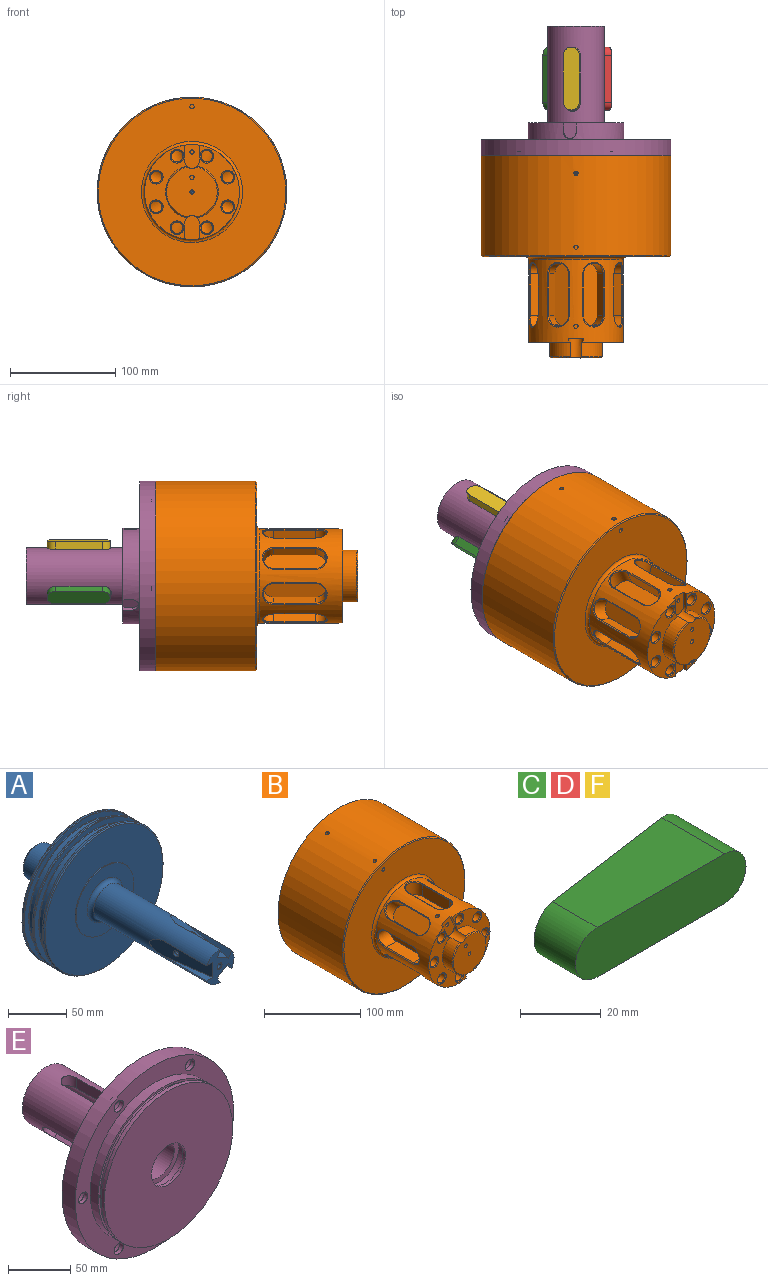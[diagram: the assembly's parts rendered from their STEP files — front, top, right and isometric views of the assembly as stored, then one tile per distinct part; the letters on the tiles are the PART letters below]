
ASSEMBLY  parts=6 mates=5
PART A: 68 faces, bbox 145x224.3x145 mm
  f0: cylinder r=1.5mm len=26.28mm, axis (0,-1,0), area 245.5mm2, adj f1,f2,f3,f4,f5,f6,f65
  f1: cylinder r=1.5mm len=11.87mm, axis (-0.99,-0.14,0), area 97.1mm2, adj f0,f4,f6,f51
  f2: cylinder r=1.5mm len=11.46mm, axis (0.5,-0.14,0.86), area 97.1mm2, adj f0,f3,f6,f55
  f3: cylinder r=1.5mm len=6.5mm, axis (-0.99,-0.14,0), area 44.4mm2, adj f0,f2,f4,f5,f6,f56
  f4: cylinder r=1.5mm len=6.81mm, axis (0.5,-0.14,0.86), area 44.4mm2, adj f0,f1,f3,f5,f6,f57
  f5: cylinder r=1.5mm len=11.46mm, axis (0.5,-0.14,-0.86), area 97.1mm2, adj f0,f3,f4,f61
  f6: cylinder r=1.5mm len=6.81mm, axis (0.5,-0.14,-0.86), area 44.4mm2, adj f0,f1,f2,f3,f4,f62
  f7: cylinder r=17.48mm len=135mm, axis (0,1,0), area 11728.8mm2, adj f8,f48,f49,f50,f52,f53,f54,f58
  f8: plane 34.95x33.06mm, normal (0,-1,0), area 511.1mm2, adj f7,f48,f49,f50,f52,f53,f54,f58
  f9: cylinder r=1.5mm len=17.25mm, axis (0,0,-1), area 153.3mm2, adj f10,f32,f36
  f10: cylinder r=17.25mm len=34.5mm, axis (0,-1,0), area 2594.2mm2, adj f9,f29,f64
  f11: cylinder r=72.5mm len=145mm, axis (0,1,0), area 774.4mm2, adj f39,f40
  f12: plane 143x143mm, normal (0,-1,0), area 12212.2mm2, adj f26,f39
  f13: plane 144x144mm, normal (0,-1,0), area 2393.1mm2, adj f42,f43
  f14: plane 144x144mm, normal (0,1,0), area 2393.1mm2, adj f40,f41
  f15: cylinder r=66mm len=132mm, axis (0,-1,0), area 3524.9mm2, adj f41,f42
  f16: cylinder r=72.5mm len=145mm, axis (0,1,0), area 728.8mm2, adj f43,f44
  f17: plane 144x144mm, normal (0,-1,0), area 2393.1mm2, adj f46,f47
  f18: plane 144x144mm, normal (0,1,0), area 2393.1mm2, adj f44,f45
  f19: cylinder r=66mm len=132mm, axis (0,-1,0), area 3524.9mm2, adj f45,f46
  f20: cylinder r=72.5mm len=145mm, axis (0,1,0), area 774.4mm2, adj f38,f47
  f21: plane 143x143mm, normal (0,1,0), area 2582.4mm2, adj f22,f38
  f22: cylinder r=65.5mm len=131mm, axis (0,-1,0), area 535mm2, adj f21,f23
  f23: plane 131x131mm, normal (0,1,0), area 3091.3mm2, adj f22,f24
  f24: cylinder r=57.5mm len=115mm, axis (0,1,0), area 2529mm2, adj f23,f25
  f25: plane 115x115mm, normal (0,1,0), area 9098.6mm2, adj f24,f64
  f26: cylinder r=35mm len=70mm, axis (0,1,0), area 219.9mm2, adj f12,f27
  f27: plane 70x70mm, normal (0,-1,0), area 2399.6mm2, adj f26,f63
  f28: cylinder r=17.48mm len=34.95mm, axis (0,1,0), area 3403.8mm2, adj f29,f31
  f29: plane 34.95x34.95mm, normal (0,-1,0), area 24.5mm2, adj f10,f28
  f30: plane 26.95x26.95mm, normal (0,1,0), area 550.8mm2, adj f31,f33
  f31: cone r=13.48mm half-angle=45deg, axis (0,-1,0), area 550mm2, adj f28,f30
  f32: cylinder r=1.5mm len=56mm, axis (0,1,0), area 518.8mm2, adj f9,f33,f35
  f33: cone r=1.5mm half-angle=45deg, axis (0,1,0), area 17.8mm2, adj f30,f32
  f34: cone r=0mm half-angle=59deg, axis (0,0,-1), area 8.2mm2, adj f35
  f35: cylinder r=1.5mm len=3mm, axis (0,0,-1), area 17.5mm2, adj f32,f34,f36
  f36: cylinder r=1.5mm len=13mm, axis (0,1,0), area 113.5mm2, adj f9,f35,f37
  f37: cone r=0mm half-angle=59deg, axis (0,1,0), area 8.2mm2, adj f36
  f38: cone r=72.5mm half-angle=45deg, axis (0,-1,0), area 639.8mm2, adj f20,f21
  f39: cone r=71.5mm half-angle=45deg, axis (0,1,0), area 639.8mm2, adj f11,f12
  f40: cone r=72.5mm half-angle=45deg, axis (0,-1,0), area 321mm2, adj f11,f14
  f41: cone r=66.5mm half-angle=45deg, axis (0,-1,0), area 294.3mm2, adj f14,f15
  f42: cone r=66mm half-angle=45deg, axis (0,1,0), area 294.3mm2, adj f13,f15
  f43: cone r=72mm half-angle=45deg, axis (0,1,0), area 321mm2, adj f13,f16
  f44: cone r=72.5mm half-angle=45deg, axis (0,-1,0), area 321mm2, adj f16,f18
  f45: cone r=66.5mm half-angle=45deg, axis (0,-1,0), area 294.3mm2, adj f18,f19
  f46: cone r=66mm half-angle=45deg, axis (0,1,0), area 294.3mm2, adj f17,f19
  f47: cone r=72mm half-angle=45deg, axis (0,1,0), area 321mm2, adj f17,f20
  f48: plane 53.99x7.59mm, normal (0,0,1), area 204.8mm2, adj f7,f8,f50
  f49: plane 53.99x7.59mm, normal (0,0,-1), area 204.8mm2, adj f7,f8,f50
  f50: plane 67.42x15.8mm, normal (-0.99,-0.14,0), area 977.6mm2, adj f7,f8,f48,f49,f51
  f51: cone r=1.5mm half-angle=45deg, axis (-0.99,-0.14,0), area 30mm2, adj f1,f50
  f52: plane 53.99x6.57mm, normal (0.87,0,-0.5), area 204.8mm2, adj f7,f8,f54
  f53: plane 53.99x6.57mm, normal (-0.87,0,0.5), area 204.8mm2, adj f7,f8,f54
  f54: plane 67.42x17.48mm, normal (0.5,-0.14,0.86), area 977.6mm2, adj f7,f8,f52,f53,f55
  f55: cone r=1.5mm half-angle=45deg, axis (0.5,-0.14,0.86), area 30mm2, adj f2,f54
  f56: cone r=0mm half-angle=59deg, axis (-0.99,-0.14,0), area 8.2mm2, adj f3
  f57: cone r=0mm half-angle=59deg, axis (0.5,-0.14,0.86), area 8.2mm2, adj f4
  f58: plane 53.99x6.57mm, normal (-0.87,0,-0.5), area 204.8mm2, adj f7,f8,f60
  f59: plane 53.99x6.57mm, normal (0.87,0,0.5), area 204.8mm2, adj f7,f8,f60
  f60: plane 67.42x17.48mm, normal (0.5,-0.14,-0.86), area 977.6mm2, adj f7,f8,f58,f59,f61
  f61: cone r=1.5mm half-angle=45deg, axis (0.5,-0.14,-0.86), area 30mm2, adj f5,f60
  f62: cone r=0mm half-angle=59deg, axis (0.5,-0.14,-0.86), area 8.2mm2, adj f6
  f63: torus R=21.48mm, axis (0,-1,0), area 747.3mm2, adj f7,f27
  f64: torus R=20.25mm, axis (0,1,0), area 543mm2, adj f10,f25
  f65: cone r=0mm half-angle=59deg, axis (0,-1,0), area 14.7mm2, adj f0,f66
  f66: cylinder r=2.5mm len=12.5mm, axis (0,-1,0), area 196.3mm2, adj f65,f67
  f67: cone r=2.5mm half-angle=45deg, axis (0,-1,0), area 12.2mm2, adj f8,f66
PART B: 156 faces, bbox 180x192x180 mm
  f0: cylinder r=2mm len=7.96mm, axis (-0.38,0,0.92), area 87.4mm2, adj f11,f123,f128
  f1: cylinder r=2mm len=41.26mm, axis (-0.38,0,0.92), area 510.5mm2, adj f2,f122,f123,f127
  f2: cylinder r=2mm len=9mm, axis (0,-1,0), area 99.3mm2, adj f1,f7,f121
  f3: cylinder r=2mm len=30mm, axis (0,-1,0), area 377mm2, adj f14,f112,f115
  f4: plane 83.39x55.54mm, normal (0,-1,0), area 1392.8mm2, adj f5,f11,f69,f80,f91,f102,f105,f106
  f5: cylinder r=25mm len=45.67mm, axis (0,1,0), area 956.4mm2, adj f4,f106,f110,f135
  f6: cylinder r=90mm len=180mm, axis (0,1,0), area 53695.6mm2, adj f9,f117,f121,f155
  f7: plane 178x178mm, normal (0,-1,0), area 17633.8mm2, adj f2,f134,f155
  f8: cylinder r=73mm len=146mm, axis (0,-1,0), area 30260.1mm2, adj f120,f132,f133
  f9: plane 180x180mm, normal (0,1,0), area 7304.2mm2, adj f6,f132,f138,f141,f144,f147,f150,f153
  f10: plane 140x140mm, normal (0,1,0), area 14318.6mm2, adj f131,f133
  f11: cylinder r=45mm len=90mm, axis (0,1,0), area 11744.7mm2, adj f0,f4,f12,f20,f21,f22,f23,f31
  f12: plane 83.39x55.54mm, normal (0,-1,0), area 1392.8mm2, adj f11,f13,f25,f36,f47,f58,f104,f106
  f13: cylinder r=25mm len=45.67mm, axis (0,1,0), area 956.4mm2, adj f12,f106,f110,f136
  f14: plane 48x48mm, normal (0,-1,0), area 1765.4mm2, adj f3,f106,f110,f111,f135,f136
  f15: cylinder r=10.1mm len=20.2mm, axis (0,0,1), area 470.9mm2, adj f16,f18,f19,f20
  f16: plane 39.8x14.84mm, normal (1,0,0), area 590.6mm2, adj f15,f17,f19,f22
  f17: cylinder r=10.1mm len=20.2mm, axis (0,0,1), area 371.8mm2, adj f16,f18,f19,f23,f24
  f18: plane 39.8x14.84mm, normal (-1,0,0), area 590.6mm2, adj f15,f17,f19,f21
  f19: plane 60x20.2mm, normal (0,0,1), area 1124.4mm2, adj f15,f16,f17,f18
  f20: bspline ~22.19x10.89mm, area 39.7mm2, adj f11,f15,f21,f22
  f21: plane 39.8x0.99mm, normal (-0.61,0,0.79), area 50mm2, adj f11,f18,f20,f23
  f22: plane 39.8x0.99mm, normal (0.61,0,0.79), area 50mm2, adj f11,f16,f20,f23
  f23: bspline ~22.18x10.89mm, area 39.7mm2, adj f11,f17,f21,f22
  f24: cylinder r=5.5mm len=14mm, axis (0,-1,0), area 483.8mm2, adj f17,f25
  f25: cone r=5.5mm half-angle=45deg, axis (0,-1,0), area 53.3mm2, adj f12,f24
  f26: cylinder r=10.1mm len=24.78mm, axis (0.71,0,0.71), area 470.9mm2, adj f27,f29,f30,f31
  f27: plane 39.8x10.49mm, normal (0.71,0,-0.71), area 590.6mm2, adj f26,f28,f30,f33
  f28: cylinder r=10.1mm len=24.78mm, axis (0.71,0,0.71), area 371.8mm2, adj f27,f29,f30,f34,f35
  f29: plane 39.8x10.49mm, normal (-0.71,0,0.71), area 590.6mm2, adj f26,f28,f30,f32
  f30: plane 60x14.28mm, normal (0.71,0,0.71), area 1124.4mm2, adj f26,f27,f28,f29
  f31: bspline ~15.69x15.69mm, area 39.7mm2, adj f11,f26,f32,f33
  f32: plane 39.8x1.25mm, normal (0.12,0,0.99), area 50mm2, adj f11,f29,f31,f34
  f33: plane 39.8x1.25mm, normal (0.99,0,0.12), area 50mm2, adj f11,f27,f31,f34
  f34: bspline ~15.69x15.69mm, area 39.7mm2, adj f11,f28,f32,f33
  f35: cylinder r=5.5mm len=14.78mm, axis (0,-1,0), area 510.7mm2, adj f28,f36
  f36: cone r=5.5mm half-angle=45deg, axis (0,-1,0), area 53.3mm2, adj f12,f35
  f37: cylinder r=10.1mm len=20.2mm, axis (1,0,0), area 470.9mm2, adj f38,f40,f41,f42
  f38: plane 39.8x14.84mm, normal (0,0,-1), area 590.6mm2, adj f37,f39,f41,f44
  f39: cylinder r=10.1mm len=20.2mm, axis (1,0,0), area 371.8mm2, adj f38,f40,f41,f45,f46
  f40: plane 39.8x14.84mm, normal (0,0,1), area 590.6mm2, adj f37,f39,f41,f43
  f41: plane 60x20.2mm, normal (1,0,0), area 1124.4mm2, adj f37,f38,f39,f40
  f42: bspline ~22.18x10.9mm, area 39.7mm2, adj f11,f37,f43,f44
  f43: plane 39.8x0.99mm, normal (0.79,0,0.61), area 50mm2, adj f11,f40,f42,f45
  f44: plane 39.8x0.99mm, normal (0.79,0,-0.61), area 50mm2, adj f11,f38,f42,f45
  f45: bspline ~22.18x10.9mm, area 39.7mm2, adj f11,f39,f43,f44
  f46: cylinder r=5.5mm len=15.63mm, axis (0,-1,0), area 540.1mm2, adj f39,f47
  f47: cone r=5.5mm half-angle=45deg, axis (0,-1,0), area 53.3mm2, adj f12,f46
  f48: cylinder r=10.1mm len=24.78mm, axis (0.71,0,-0.71), area 470.9mm2, adj f49,f51,f52,f53
  f49: plane 39.8x10.49mm, normal (-0.71,0,-0.71), area 590.6mm2, adj f48,f50,f52,f55
  f50: cylinder r=10.1mm len=24.78mm, axis (0.71,0,-0.71), area 371.9mm2, adj f49,f51,f52,f56,f57
  f51: plane 39.8x10.49mm, normal (0.71,0,0.71), area 590.6mm2, adj f48,f50,f52,f54
  f52: plane 60x14.28mm, normal (0.71,0,-0.71), area 1124.4mm2, adj f48,f49,f50,f51
  f53: bspline ~15.69x15.69mm, area 39.7mm2, adj f11,f48,f54,f55
  f54: plane 39.8x1.25mm, normal (0.99,0,-0.12), area 50mm2, adj f11,f51,f53,f56
  f55: plane 39.8x1.25mm, normal (0.12,0,-0.99), area 50mm2, adj f11,f49,f53,f56
  f56: bspline ~15.69x15.69mm, area 39.7mm2, adj f11,f50,f54,f55
  f57: cylinder r=5.5mm len=14.78mm, axis (0,-1,0), area 510.7mm2, adj f50,f58
  f58: cone r=5.5mm half-angle=45deg, axis (0,-1,0), area 53.3mm2, adj f12,f57
  f59: cylinder r=10.1mm len=20.2mm, axis (0,0,-1), area 470.9mm2, adj f60,f62,f63,f64
  f60: plane 39.8x14.84mm, normal (-1,0,0), area 590.6mm2, adj f59,f61,f63,f66
  f61: cylinder r=10.1mm len=20.2mm, axis (0,0,-1), area 371.9mm2, adj f60,f62,f63,f67,f68
  f62: plane 39.8x14.84mm, normal (1,0,0), area 590.6mm2, adj f59,f61,f63,f65
  f63: plane 60x20.2mm, normal (0,0,-1), area 1124.4mm2, adj f59,f60,f61,f62
  f64: bspline ~22.18x10.9mm, area 39.7mm2, adj f11,f59,f65,f66
  f65: plane 39.8x0.99mm, normal (0.61,0,-0.79), area 50mm2, adj f11,f62,f64,f67
  f66: plane 39.8x0.99mm, normal (-0.61,0,-0.79), area 50mm2, adj f11,f60,f64,f67
  f67: bspline ~22.18x10.9mm, area 39.7mm2, adj f11,f61,f65,f66
  f68: cylinder r=5.5mm len=14mm, axis (0,-1,0), area 483.8mm2, adj f61,f69
  f69: cone r=5.5mm half-angle=45deg, axis (0,-1,0), area 53.3mm2, adj f4,f68
  f70: cylinder r=10.1mm len=24.78mm, axis (-0.71,0,-0.71), area 470.9mm2, adj f71,f73,f74,f75
  f71: plane 39.8x10.49mm, normal (-0.71,0,0.71), area 590.6mm2, adj f70,f72,f74,f77
  f72: cylinder r=10.1mm len=24.78mm, axis (-0.71,0,-0.71), area 372mm2, adj f71,f73,f74,f78,f79
  f73: plane 39.8x10.49mm, normal (0.71,0,-0.71), area 590.6mm2, adj f70,f72,f74,f76
  f74: plane 60x14.28mm, normal (-0.71,0,-0.71), area 1124.4mm2, adj f70,f71,f72,f73
  f75: bspline ~15.69x15.69mm, area 39.7mm2, adj f11,f70,f76,f77
  f76: plane 39.8x1.25mm, normal (-0.12,0,-0.99), area 50mm2, adj f11,f73,f75,f78
  f77: plane 39.8x1.25mm, normal (-0.99,0,-0.12), area 50mm2, adj f11,f71,f75,f78
  f78: bspline ~15.69x15.69mm, area 39.7mm2, adj f11,f72,f76,f77
  f79: cylinder r=5.5mm len=14.78mm, axis (0,-1,0), area 510.7mm2, adj f72,f80
  f80: cone r=5.5mm half-angle=45deg, axis (0,-1,0), area 53.3mm2, adj f4,f79
  f81: cylinder r=10.1mm len=20.2mm, axis (-1,0,0), area 470.9mm2, adj f82,f84,f85,f86
  f82: plane 39.8x14.84mm, normal (0,0,1), area 590.6mm2, adj f81,f83,f85,f88
  f83: cylinder r=10.1mm len=20.2mm, axis (-1,0,0), area 372mm2, adj f82,f84,f85,f89,f90
  f84: plane 39.8x14.84mm, normal (0,0,-1), area 590.6mm2, adj f81,f83,f85,f87
  f85: plane 60x20.2mm, normal (-1,0,0), area 1124.4mm2, adj f81,f82,f83,f84
  f86: bspline ~22.18x10.9mm, area 39.7mm2, adj f11,f81,f87,f88
  f87: plane 39.8x0.99mm, normal (-0.79,0,-0.61), area 50mm2, adj f11,f84,f86,f89
  f88: plane 39.8x0.99mm, normal (-0.79,0,0.61), area 50mm2, adj f11,f82,f86,f89
  f89: bspline ~22.18x10.9mm, area 39.7mm2, adj f11,f83,f87,f88
  f90: cylinder r=5.5mm len=15.63mm, axis (0,-1,0), area 540.1mm2, adj f83,f91
  f91: cone r=5.5mm half-angle=45deg, axis (0,-1,0), area 53.3mm2, adj f4,f90
  f92: cylinder r=10.1mm len=24.78mm, axis (-0.71,0,0.71), area 470.9mm2, adj f93,f95,f96,f97
  f93: plane 39.8x10.49mm, normal (0.71,0,0.71), area 590.6mm2, adj f92,f94,f96,f99
  f94: cylinder r=10.1mm len=24.78mm, axis (-0.71,0,0.71), area 371.9mm2, adj f93,f95,f96,f100,f101
  f95: plane 39.8x10.49mm, normal (-0.71,0,-0.71), area 590.6mm2, adj f92,f94,f96,f98
  f96: plane 60x14.28mm, normal (-0.71,0,0.71), area 1124.4mm2, adj f92,f93,f94,f95
  f97: bspline ~15.69x15.69mm, area 39.7mm2, adj f11,f92,f98,f99
  f98: plane 39.8x1.25mm, normal (-0.99,0,0.12), area 50mm2, adj f11,f95,f97,f100
  f99: plane 39.8x1.25mm, normal (-0.12,0,0.99), area 50mm2, adj f11,f93,f97,f100
  f100: bspline ~15.69x15.69mm, area 39.7mm2, adj f11,f94,f98,f99
  f101: cylinder r=5.5mm len=14.78mm, axis (0,-1,0), area 510.7mm2, adj f94,f102
  f102: cone r=5.5mm half-angle=45deg, axis (0,-1,0), area 53.3mm2, adj f4,f101
  f103: plane 23.68x19.27mm, normal (0,-1,0), area 281.7mm2, adj f11,f104,f105,f106,f128
  f104: plane 14x5.8mm, normal (-0.92,0,-0.38), area 53mm2, adj f11,f12,f103,f106
  f105: plane 14x5.8mm, normal (0.92,0,0.38), area 53mm2, adj f4,f11,f103,f106
  f106: cylinder r=7mm len=18.5mm, axis (0,-1,0), area 246mm2, adj f4,f5,f12,f13,f14,f103,f104,f105
  f107: plane 23.68x19.27mm, normal (0,-1,0), area 294.2mm2, adj f11,f108,f109,f110
  f108: plane 14x5.8mm, normal (0.92,0,0.38), area 53mm2, adj f4,f11,f107,f110
  f109: plane 14x5.8mm, normal (-0.92,0,-0.38), area 53mm2, adj f11,f12,f107,f110
  f110: cylinder r=7mm len=18.5mm, axis (0,-1,0), area 246mm2, adj f4,f5,f12,f13,f14,f107,f108,f109
  f111: cylinder r=2mm len=56mm, axis (0,-1,0), area 703.7mm2, adj f14,f129
  f112: cylinder r=2mm len=23.7mm, axis (-0.38,0,0.92), area 271.8mm2, adj f3,f114,f123,f128
  f113: plane 4x4mm, normal (0,-1,0), area 12.6mm2, adj f114
  f114: cylinder r=2mm len=5mm, axis (0,-1,0), area 62.8mm2, adj f112,f113,f115
  f115: cylinder r=2mm len=4.77mm, axis (-0.38,0,0.92), area 19.2mm2, adj f3,f114,f116
  f116: plane 4x3.7mm, normal (-0.38,0,0.92), area 12.6mm2, adj f115
  f117: cylinder r=2mm len=9.83mm, axis (-0.38,0,0.92), area 112.8mm2, adj f6,f119,f122
  f118: plane 4x4mm, normal (0,-1,0), area 12.6mm2, adj f119
  f119: cylinder r=2mm len=5mm, axis (0,-1,0), area 62.8mm2, adj f117,f118,f120
  f120: cylinder r=2mm len=8.95mm, axis (-0.38,0,0.92), area 100.9mm2, adj f8,f119,f122
  f121: cylinder r=2mm len=9.83mm, axis (-0.38,0,0.92), area 112.8mm2, adj f2,f6,f122
  f122: cylinder r=2mm len=70mm, axis (0,-1,0), area 879.6mm2, adj f1,f117,f120,f121
  f123: cylinder r=2mm len=75mm, axis (0,-1,0), area 942.5mm2, adj f0,f1,f112,f125
  f124: plane 4x3.7mm, normal (-0.38,0,0.92), area 12.6mm2, adj f125
  f125: cylinder r=2mm len=5.15mm, axis (-0.38,0,0.92), area 31.8mm2, adj f123,f124,f127
  f126: plane 4x4mm, normal (0,-1,0), area 12.6mm2, adj f127
  f127: cylinder r=2mm len=5mm, axis (0,-1,0), area 62.8mm2, adj f1,f125,f126
  f128: cylinder r=2mm len=11.5mm, axis (0,-1,0), area 130.7mm2, adj f0,f103,f112
  f129: plane 35x35mm, normal (0,1,0), area 949.5mm2, adj f111,f130
  f130: cylinder r=17.5mm len=56mm, axis (0,1,0), area 6157.5mm2, adj f129,f131
  f131: cone r=18.5mm half-angle=14deg, axis (0,1,0), area 466.3mm2, adj f10,f130
  f132: cone r=75mm half-angle=15.9deg, axis (0,1,0), area 3384.9mm2, adj f8,f9
  f133: torus R=70mm, axis (0,-1,0), area 2129.2mm2, adj f8,f10
  f134: torus R=48mm, axis (0,-1,0), area 1364.7mm2, adj f7,f11
  f135: cone r=24mm half-angle=45deg, axis (0,1,0), area 95.8mm2, adj f5,f14,f106,f110
  f136: cone r=24mm half-angle=45deg, axis (0,1,0), area 95.8mm2, adj f13,f14,f106,f110
  f137: cylinder r=4.3mm len=36.3mm, axis (0,1,0), area 980.7mm2, adj f138,f139
  f138: cone r=4.3mm half-angle=45deg, axis (0,1,0), area 28.9mm2, adj f9,f137
  f139: cone r=0mm half-angle=59deg, axis (0,1,0), area 67.8mm2, adj f137
  f140: cylinder r=4.3mm len=36.3mm, axis (0,1,0), area 980.7mm2, adj f141,f142
  f141: cone r=4.3mm half-angle=45deg, axis (0,1,0), area 28.9mm2, adj f9,f140
  f142: cone r=0mm half-angle=59deg, axis (0,1,0), area 67.8mm2, adj f140
  f143: cylinder r=4.3mm len=36.3mm, axis (0,1,0), area 980.7mm2, adj f144,f145
  f144: cone r=4.3mm half-angle=45deg, axis (0,1,0), area 28.9mm2, adj f9,f143
  f145: cone r=0mm half-angle=59deg, axis (0,1,0), area 67.8mm2, adj f143
  f146: cylinder r=4.3mm len=36.3mm, axis (0,1,0), area 980.7mm2, adj f147,f148
  f147: cone r=4.3mm half-angle=45deg, axis (0,1,0), area 28.9mm2, adj f9,f146
  f148: cone r=0mm half-angle=59deg, axis (0,1,0), area 67.8mm2, adj f146
  f149: cylinder r=4.3mm len=36.3mm, axis (0,1,0), area 980.7mm2, adj f150,f151
  f150: cone r=4.3mm half-angle=45deg, axis (0,1,0), area 28.9mm2, adj f9,f149
  f151: cone r=0mm half-angle=59deg, axis (0,1,0), area 67.8mm2, adj f149
  f152: cylinder r=4.3mm len=36.3mm, axis (0,1,0), area 980.7mm2, adj f153,f154
  f153: cone r=4.3mm half-angle=45deg, axis (0,1,0), area 28.9mm2, adj f9,f152
  f154: cone r=0mm half-angle=59deg, axis (0,1,0), area 67.8mm2, adj f152
  f155: cone r=89mm half-angle=45deg, axis (0,1,0), area 795.3mm2, adj f6,f7
PART C: 6 faces, bbox 59.8x23x15.1 mm
  f0: cylinder r=7.55mm len=23mm, axis (0,1,0), area 536.4mm2, adj f1,f3,f4,f5
  f1: plane 44.7x21.94mm, normal (0,0,1), area 840.3mm2, adj f0,f2,f4,f5
  f2: cylinder r=7.55mm len=15.66mm, axis (0,1,0), area 355.3mm2, adj f1,f3,f4,f5
  f3: plane 44.7x21.94mm, normal (0,0,-1), area 840.3mm2, adj f0,f2,f4,f5
  f4: plane 59.8x15.1mm, normal (0,-1,0), area 854mm2, adj f0,f1,f2,f3
  f5: plane 59.8x15.1mm, normal (-0.14,0.99,0), area 862.4mm2, adj f0,f1,f2,f3
PART D: same geometry as C
PART E: 68 faces, bbox 180x139x180 mm
  f0: cylinder r=72.95mm len=145.9mm, axis (0,1,0), area 1604.3mm2, adj f5,f63
  f1: cylinder r=72.95mm len=145.9mm, axis (0,1,0), area 4125.2mm2, adj f3,f65
  f2: cylinder r=90mm len=180mm, axis (0,1,0), area 8482.3mm2, adj f3,f4
  f3: plane 180x180mm, normal (0,-1,0), area 8208.7mm2, adj f1,f2,f45,f48,f51,f54,f57,f60
  f4: plane 180x180mm, normal (0,1,0), area 17581.1mm2, adj f2,f6,f47,f50,f53,f56,f59,f62
  f5: plane 145.9x145.9mm, normal (0,-1,0), area 15533.2mm2, adj f0,f10
  f6: cylinder r=45.5mm len=91mm, axis (0,-1,0), area 4071.4mm2, adj f4,f7,f33,f34,f35,f37,f38,f39
  f7: plane 91x90.59mm, normal (0,1,0), area 2717.1mm2, adj f6,f31,f33,f35,f36,f37,f39,f40
  f8: plane 54x54mm, normal (0,1,0), area 1286.5mm2, adj f9,f12,f14,f16,f18
  f9: cylinder r=27mm len=96mm, axis (0,-1,0), area 13654.1mm2, adj f8,f19,f20,f21,f22,f23,f24,f25
  f10: cylinder r=19.43mm len=38.85mm, axis (0,-1,0), area 366.2mm2, adj f5,f66
  f11: plane 45x45mm, normal (0,-1,0), area 628.3mm2, adj f12,f67
  f12: cylinder r=17.5mm len=128mm, axis (0,1,0), area 11393mm2, adj f8,f11,f19,f20,f21,f22,f23,f24
  f13: cone r=0mm half-angle=59deg, axis (0,1,0), area 16.2mm2, adj f14
  f14: cylinder r=2.1mm len=20mm, axis (0,1,0), area 263.9mm2, adj f8,f13
  f15: cone r=0mm half-angle=59deg, axis (0,1,0), area 16.2mm2, adj f16
  f16: cylinder r=2.1mm len=20mm, axis (0,1,0), area 263.9mm2, adj f8,f15
  f17: cone r=0mm half-angle=59deg, axis (0,1,0), area 16.2mm2, adj f18
  f18: cylinder r=2.1mm len=20mm, axis (0,1,0), area 263.9mm2, adj f8,f17
  f19: cylinder r=7.5mm len=18.58mm, axis (-0.87,0,0.5), area 232.9mm2, adj f9,f12,f20,f22
  f20: plane 46.23x8.77mm, normal (0.5,0,0.87), area 468.1mm2, adj f9,f12,f19,f21
  f21: cylinder r=7.5mm len=18.59mm, axis (-0.87,0,0.5), area 231.1mm2, adj f9,f12,f20,f22
  f22: plane 45.59x8.77mm, normal (-0.5,0,-0.87), area 461.6mm2, adj f9,f12,f19,f21
  f23: cylinder r=7.5mm len=18.58mm, axis (0.87,0,0.5), area 232.9mm2, adj f9,f12,f24,f26
  f24: plane 46.23x8.77mm, normal (0.5,0,-0.87), area 468.1mm2, adj f9,f12,f23,f25
  f25: cylinder r=7.5mm len=18.59mm, axis (0.87,0,0.5), area 231.1mm2, adj f9,f12,f24,f26
  f26: plane 45.59x8.78mm, normal (-0.5,0,0.87), area 461.6mm2, adj f9,f12,f23,f25
  f27: cylinder r=7.5mm len=15mm, axis (0,0,-1), area 232.9mm2, adj f9,f12,f28,f30
  f28: plane 46.23x10.13mm, normal (-1,0,0), area 468.1mm2, adj f9,f12,f27,f29
  f29: cylinder r=7.5mm len=15mm, axis (0,0,-1), area 231mm2, adj f9,f12,f28,f30
  f30: plane 45.59x10.13mm, normal (1,0,0), area 461.6mm2, adj f9,f12,f27,f29
  f31: cylinder r=34mm len=68mm, axis (0,1,0), area 854.5mm2, adj f7,f32
  f32: plane 68x68mm, normal (0,1,0), area 1341.5mm2, adj f9,f31
  f33: plane 8.9x3.43mm, normal (0.5,0,0.87), area 35.3mm2, adj f6,f7,f34,f36
  f34: cylinder r=6.1mm len=12.75mm, axis (-0.87,0,0.5), area 79.9mm2, adj f6,f33,f35,f36
  f35: plane 8.9x3.43mm, normal (-0.5,0,-0.87), area 35.3mm2, adj f6,f7,f34,f36
  f36: plane 15x10.57mm, normal (0.87,0,-0.5), area 167mm2, adj f7,f33,f34,f35
  f37: plane 8.9x3.96mm, normal (-1,0,0), area 35.3mm2, adj f6,f7,f38,f40
  f38: cylinder r=6.1mm len=12.2mm, axis (0,0,-1), area 79.9mm2, adj f6,f37,f39,f40
  f39: plane 8.9x3.96mm, normal (1,0,0), area 35.3mm2, adj f6,f7,f38,f40
  f40: plane 15x12.2mm, normal (0,0,1), area 167mm2, adj f7,f37,f38,f39
  f41: plane 8.9x3.43mm, normal (0.5,0,-0.87), area 35.3mm2, adj f6,f7,f42,f44
  f42: cylinder r=6.1mm len=12.75mm, axis (0.87,0,0.5), area 79.9mm2, adj f6,f41,f43,f44
  f43: plane 8.9x3.43mm, normal (-0.5,0,0.87), area 35.3mm2, adj f6,f7,f42,f44
  f44: plane 15x10.57mm, normal (-0.87,0,-0.5), area 167mm2, adj f7,f41,f42,f43
  f45: cylinder r=5.25mm len=10.5mm, axis (0,1,0), area 131.9mm2, adj f3,f46
  f46: plane 17x17mm, normal (0,1,0), area 140.4mm2, adj f45,f47
  f47: cylinder r=8.5mm len=17mm, axis (0,1,0), area 587.5mm2, adj f4,f46
  f48: cylinder r=5.25mm len=10.5mm, axis (0,1,0), area 131.9mm2, adj f3,f49
  f49: plane 17x17mm, normal (0,1,0), area 140.4mm2, adj f48,f50
  f50: cylinder r=8.5mm len=17mm, axis (0,1,0), area 587.5mm2, adj f4,f49
  f51: cylinder r=5.25mm len=10.5mm, axis (0,1,0), area 131.9mm2, adj f3,f52
  f52: plane 17x17mm, normal (0,1,0), area 140.4mm2, adj f51,f53
  f53: cylinder r=8.5mm len=17mm, axis (0,1,0), area 587.5mm2, adj f4,f52
  f54: cylinder r=5.25mm len=10.5mm, axis (0,1,0), area 131.9mm2, adj f3,f55
  f55: plane 17x17mm, normal (0,1,0), area 140.4mm2, adj f54,f56
  f56: cylinder r=8.5mm len=17mm, axis (0,1,0), area 587.5mm2, adj f4,f55
  f57: cylinder r=5.25mm len=10.5mm, axis (0,1,0), area 131.9mm2, adj f3,f58
  f58: plane 17x17mm, normal (0,1,0), area 140.4mm2, adj f57,f59
  f59: cylinder r=8.5mm len=17mm, axis (0,1,0), area 587.5mm2, adj f4,f58
  f60: cylinder r=5.25mm len=10.5mm, axis (0,1,0), area 131.9mm2, adj f3,f61
  f61: plane 17x17mm, normal (0,1,0), area 140.4mm2, adj f60,f62
  f62: cylinder r=8.5mm len=17mm, axis (0,1,0), area 587.5mm2, adj f4,f61
  f63: plane 145.9x145.9mm, normal (0,1,0), area 904.2mm2, adj f0,f64
  f64: cylinder r=70.95mm len=141.9mm, axis (0,-1,0), area 1560.3mm2, adj f63,f65
  f65: plane 145.9x145.9mm, normal (0,-1,0), area 904.2mm2, adj f1,f64
  f66: plane 45x45mm, normal (0,1,0), area 405mm2, adj f10,f67
  f67: cylinder r=22.5mm len=45mm, axis (0,1,0), area 1131mm2, adj f11,f66
PART F: same geometry as C
PLACE A rot(axis=(0.2,0,0.98),180deg) t=(-2.66,145.5,-25.97)mm
PLACE B rot(axis=(0,1,0),22.5deg) t=(-2.66,116,-25.97)mm fixed
PLACE C rot(axis=(0.69,0.69,0.23),153.7deg) t=(-11.21,270.71,-32.53)mm
PLACE D rot(axis=(0.19,0.19,0.96),92.2deg) t=(7.3,270.71,-30.1)mm
PLACE E rot(axis=(0,1,0),112.5deg) t=(-2.66,207,-25.97)mm
PLACE F rot(axis=(-0.6,-0.6,0.53),124.4deg) t=(-4.07,270.71,-15.29)mm
MATE fastened E.f10 <-> B.f5  axis (0,-1,0) through (-2.66,192,-25.97)mm
MATE slider A.f28 <-> B.f111  axis (0,-1,0) through (-2.66,110,-25.97)mm
MATE slider C.f0 <-> E.f19  axis (0.79,0,0.61) through (-20.28,287.5,-39.49)mm
MATE slider D.f0 <-> E.f27  axis (-0.92,0,0.38) through (17.86,287.5,-34.47)mm
MATE slider F.f0 <-> E.f23  axis (0.13,0,-0.99) through (-4.05,287.5,-15.43)mm
